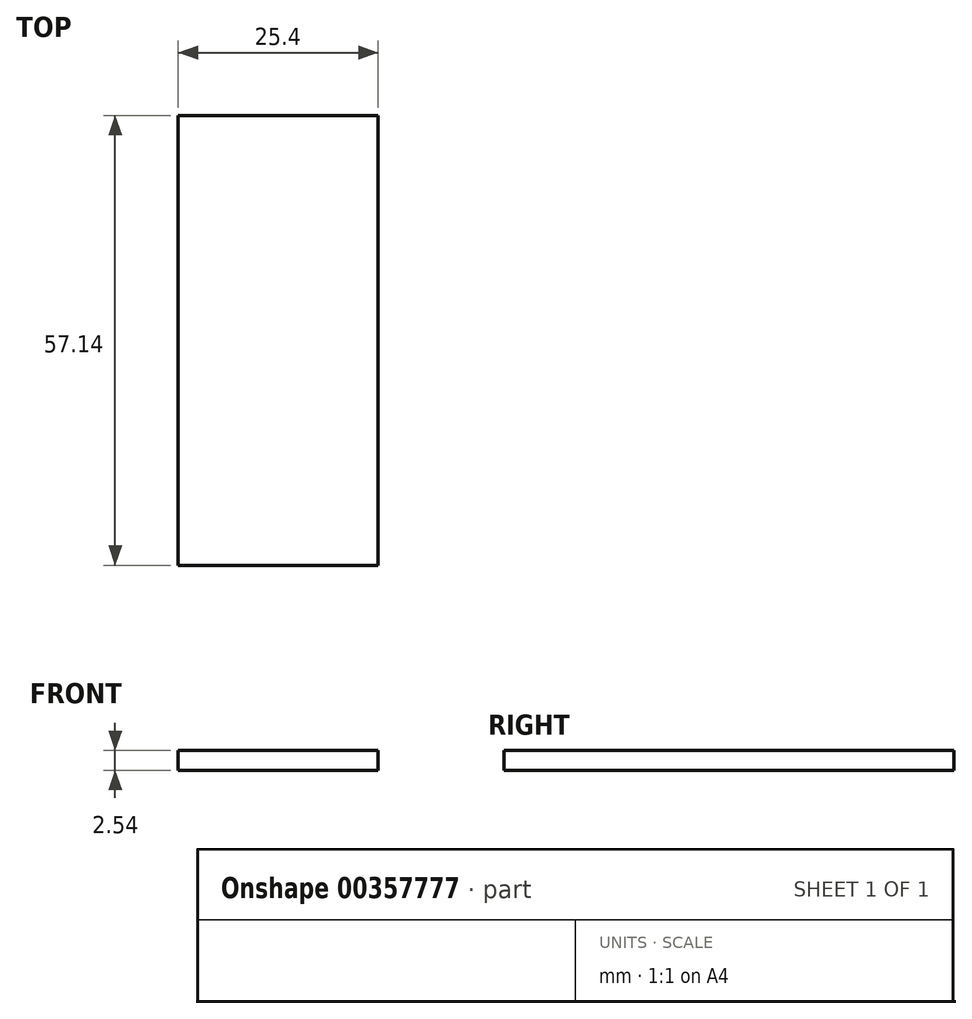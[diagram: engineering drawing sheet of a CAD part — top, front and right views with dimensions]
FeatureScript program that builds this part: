
annotation { "Feature Type Name" : "Feature", "Feature Type Description" : "" }
export const myFeature = defineFeature(function(context is Context, id is Id, definition is map)
    precondition{}
    {
        {
            var Q0;
            Q0=qCreatedBy(makeId("Top.planeOp"),FACE);
            var sketch = newSketch(context, id + "F0", { "sketchPlane" : qUnion([Q0])});
            skLineSegment(sketch, "E0.bottom", {"start": v(12.7, -28.58) * mm, "end": v(-12.7, -28.58) * mm});
            skLineSegment(sketch, "E0.top", {"start": v(12.7, 28.58) * mm, "end": v(-12.7, 28.58) * mm});
            skLineSegment(sketch, "E0.left", {"start": v(12.7, -28.58) * mm, "end": v(12.7, 28.58) * mm});
            skLineSegment(sketch, "E0.right", {"start": v(-12.7, -28.58) * mm, "end": v(-12.7, 28.57) * mm});
            skPoint(sketch, "E0.middle", {"position": v(0, 0) * mm});
            skSolve(sketch);
        }
        {
            var Q0;
            Q0=makeQuery(id+"F0.imprint","IMPRINT",FACE,{"disambiguationData":[TD([[makeQuery(id+"F0.imprint","IMPRINT",EDGE,{"derivedFrom":sQuery(id+"F0.wireOp",EDGE,"E0.bottom")}),-1.0]])]});
            extrude(context, id + "F1", {"entities" : qUnion([Q0]), "depth" : 2.54 * mm});
        }
    });
